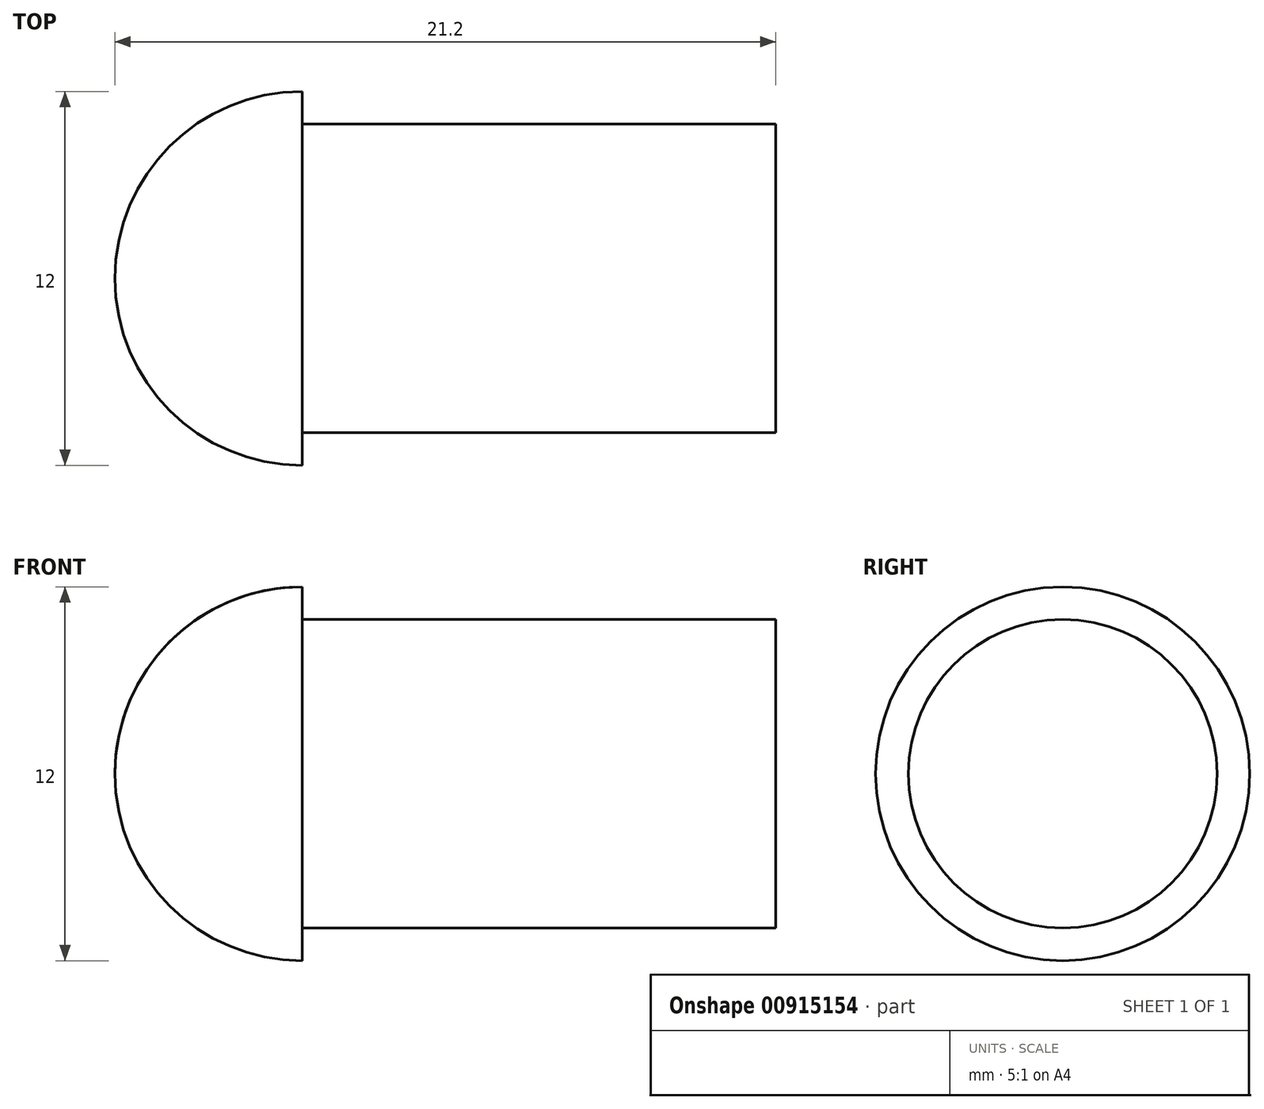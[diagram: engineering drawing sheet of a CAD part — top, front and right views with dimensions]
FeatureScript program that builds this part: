
annotation { "Feature Type Name" : "Feature", "Feature Type Description" : "" }
export const myFeature = defineFeature(function(context is Context, id is Id, definition is map)
    precondition{}
    {
        {
            var Q0;
            Q0=qCreatedBy(makeId("Front.planeOp"),FACE);
            var sketch = newSketch(context, id + "F0", { "sketchPlane" : qUnion([Q0])});
            skLineSegment(sketch, "E0.bottom", {"start": v(7.6, -4.95) * mm, "end": v(-7.6, -4.95) * mm});
            skLineSegment(sketch, "E0.top", {"start": v(7.6, 4.95) * mm, "end": v(-7.6, 4.95) * mm});
            skLineSegment(sketch, "E0.left", {"start": v(7.6, -4.95) * mm, "end": v(7.6, 4.95) * mm});
            skLineSegment(sketch, "E0.right", {"start": v(-7.6, -4.95) * mm, "end": v(-7.6, 4.95) * mm});
            skPoint(sketch, "E0.middle", {"position": v(0, 0) * mm});
            skLineSegment(sketch, "E1", {"start": v(-7.6, 0) * mm, "end": v(-13.6, 0) * mm});
            skLineSegment(sketch, "E2", {"start": v(-7.6, 0) * mm, "end": v(-7.6, 6) * mm});
            skLineSegment(sketch, "E3", {"start": v(-7.6, 0) * mm, "end": v(-7.6, -6) * mm});
            skArc(sketch, "E4", {"start": v(-13.6, 0) * mm, "mid": v(-11.84, -4.24) * mm, "end": v(-7.6, -6) * mm});
            skArc(sketch, "E5", {"start": v(-13.6, 0) * mm, "mid": v(-11.84, 4.24) * mm, "end": v(-7.6, 6) * mm});
            skLineSegment(sketch, "E6", {"start": v(7.6, 0) * mm, "end": v(7.6, 6) * mm});
            skLineSegment(sketch, "E7", {"start": v(7.6, 0) * mm, "end": v(7.6, -6) * mm});
            skLineSegment(sketch, "E8", {"start": v(7.6, 0) * mm, "end": v(13.6, 0) * mm});
            skArc(sketch, "E9", {"start": v(13.6, 0) * mm, "mid": v(11.84, 4.24) * mm, "end": v(7.6, 6) * mm});
            skArc(sketch, "E10", {"start": v(13.6, 0) * mm, "mid": v(11.84, -4.24) * mm, "end": v(7.6, -6) * mm});
            skLineSegment(sketch, "E11", {"start": v(-7.6, 0) * mm, "end": v(7.6, 0) * mm});
            skLineSegment(sketch, "E12", {"start": v(-13.6, 0) * mm, "end": v(13.6, 0) * mm});
            skSolve(sketch);
        }
        {
            var Q0;
            {var subQ0=sQuery(id+"F0.wireOp",EDGE,"E0.bottom");Q0=makeQuery(id+"F0.imprint","IMPRINT",FACE,{"disambiguationData":[TD([[makeQuery(id+"F0.imprint","IMPRINT",EDGE,{"derivedFrom":subQ0}),-1.0]])]});}
            var Q1;
            {var subQ4=sQuery(id+"F0.wireOp",EDGE,"E10");Q1=makeQuery(id+"F0.imprint","IMPRINT",FACE,{"disambiguationData":[TD([[makeQuery(id+"F0.imprint","IMPRINT",EDGE,{"derivedFrom":subQ4}),-1.0]])]});}
            var Q2;
            {var subQ4=sQuery(id+"F0.wireOp",EDGE,"E4");Q2=makeQuery(id+"F0.imprint","IMPRINT",FACE,{"disambiguationData":[TD([[makeQuery(id+"F0.imprint","IMPRINT",EDGE,{"derivedFrom":subQ4}),1.0]])]});}
            var Q3;
            Q3=sQuery(id+"F0.wireOp",EDGE,"E11");
            revolve(context, id + "F1", {"surfaceOperationType" : NewSurfaceOperationType.NEW, "entities" : qUnion([Q0, Q1, Q2]), "axis" : qUnion([Q3]), "revolveType" : RevolveType.FULL});
        }
    });
